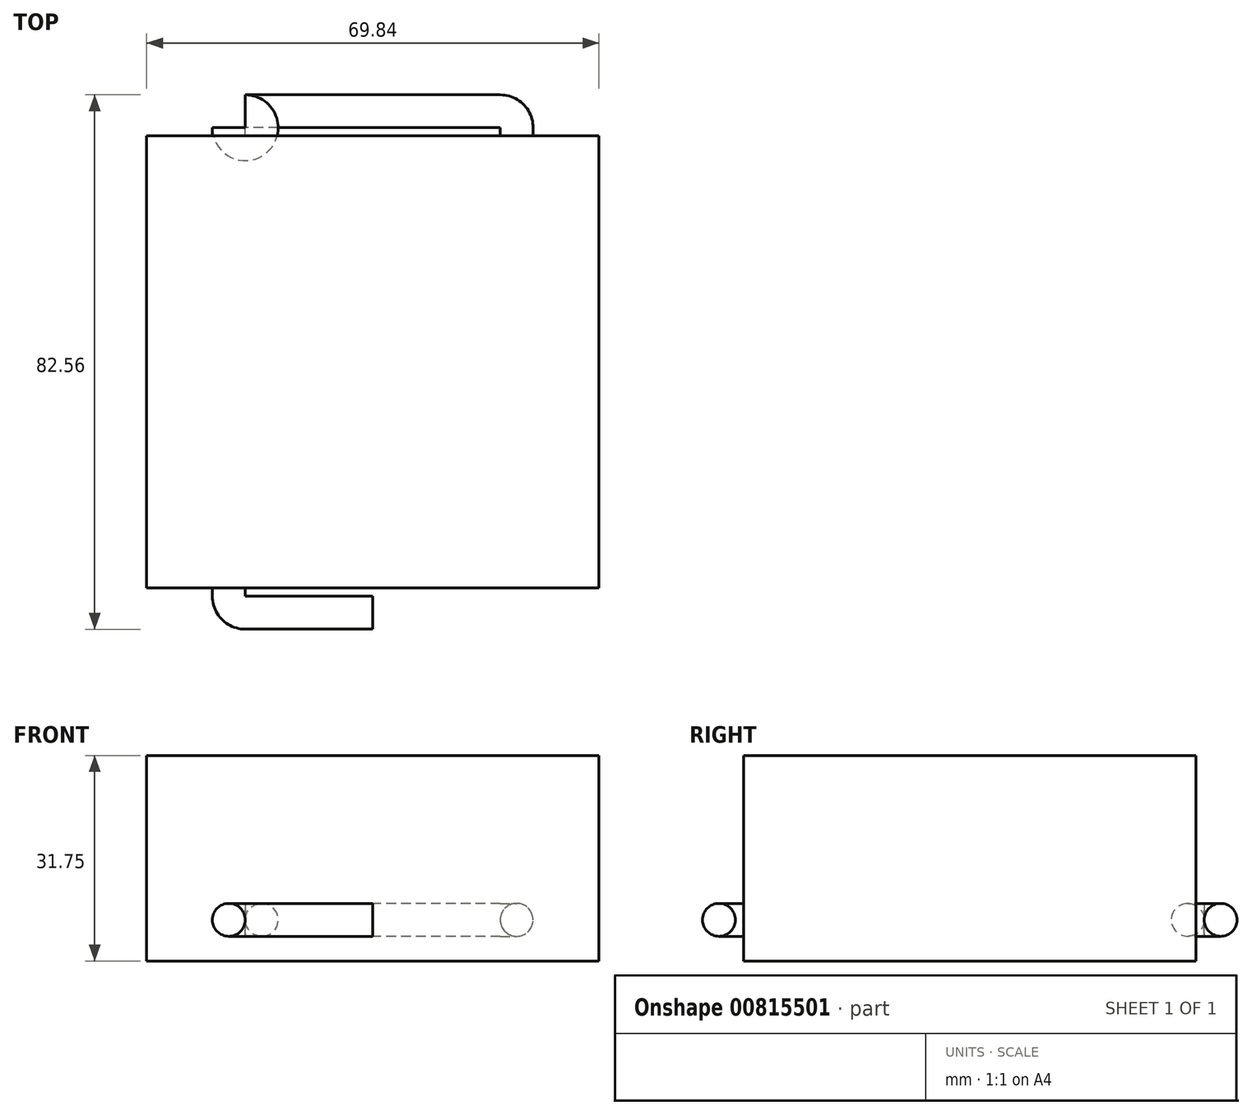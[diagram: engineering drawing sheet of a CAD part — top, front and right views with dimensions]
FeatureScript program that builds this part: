
annotation { "Feature Type Name" : "Feature", "Feature Type Description" : "" }
export const myFeature = defineFeature(function(context is Context, id is Id, definition is map)
    precondition{}
    {
        {
            var Q0;
            Q0=qCreatedBy(makeId("Top.planeOp"),FACE);
            var sketch = newSketch(context, id + "F0", { "sketchPlane" : qUnion([Q0])});
            skLineSegment(sketch, "E0.bottom", {"start": v(34.93, -34.92) * mm, "end": v(-34.92, -34.93) * mm});
            skLineSegment(sketch, "E0.top", {"start": v(34.92, 34.93) * mm, "end": v(-34.93, 34.93) * mm});
            skLineSegment(sketch, "E0.left", {"start": v(34.93, -34.92) * mm, "end": v(34.92, 34.93) * mm});
            skLineSegment(sketch, "E0.right", {"start": v(-34.92, -34.93) * mm, "end": v(-34.93, 34.93) * mm});
            skPoint(sketch, "E0.middle", {"position": v(0, 0) * mm});
            skSolve(sketch);
        }
        {
            var Q0;
            Q0 = qSketchRegion(id + "F0", true);
            extrude(context, id + "F1", {"entities" : qUnion([Q0]), "depth" : 31.75 * mm, "offsetDistance" : 25.4 * mm});
        }
        {
            var Q0;
            Q0=qCreatedBy(makeId("Top.planeOp"),FACE);
            cPlane(context, id + "F2", {"entities" : qUnion([Q0]), "cplaneType" : CPlaneType.OFFSET, "offset" : 6.35 * mm, "width" : 152.4 * mm, "height" : 152.4 * mm});
        }
        {
            var Q0;
            Q0=qCreatedBy(id+"F2.planeOp",FACE);
            var sketch = newSketch(context, id + "F3", { "sketchPlane" : qUnion([Q0])});
            skLineSegment(sketch, "E1", {"start": v(0, 0) * mm, "end": v(0, 38.73) * mm, "construction": true});
            skLineSegment(sketch, "E2", {"start": v(0, 38.73) * mm, "end": v(19.69, 38.73) * mm});
            skLineSegment(sketch, "E3", {"start": v(22.23, 36.2) * mm, "end": v(22.23, 34.92) * mm});
            skPoint(sketch, "E4.visualSharp", {"position": v(22.23, 38.73) * mm});
            skArc(sketch, "E4.filletArc", {"start": v(22.23, 36.2) * mm, "mid": v(21.48, 38) * mm, "end": v(19.69, 38.73) * mm});
            skSolve(sketch);
        }
        {
            var Q0;
            Q0=makeQuery(id+"F1.opExtrude","SWEPT_FACE",FACE,{"disambiguationData":[OSD([sQuery(id+"F0.wireOp",EDGE,"E0.top")])]});
            var sketch = newSketch(context, id + "F4", { "sketchPlane" : qUnion([Q0])});
            skLineSegment(sketch, "E5", {"start": v(0, 0) * mm, "end": v(0, 6.35) * mm, "construction": true});
            skLineSegment(sketch, "E6", {"start": v(0, 6.35) * mm, "end": v(-22.23, 6.35) * mm, "construction": true});
            skCircle(sketch, "E7", {"center": v(-22.23, 6.35) * mm, "radius": 2.54 * mm});
            skSolve(sketch);
        }
        {
            var Q0;
            Q0=makeQuery(id+"F4.imprint","IMPRINT",FACE,{"disambiguationData":[TD([[makeQuery(id+"F4.imprint","IMPRINT",EDGE,{"derivedFrom":sQuery(id+"F4.wireOp",EDGE,"E7")}),1.0]])]});
            var Q1;
            Q1 = qConstructionFilter(qBodyType(qCreatedBy(id + "F3" ,EDGE), BodyType.WIRE), ConstructionObject.NO);
            sweep(context, id + "F5", {"operationType" : NewBodyOperationType.ADD, "profiles" : qUnion([Q0]), "path" : qUnion([Q1])});
        }
        {
            var Q0;
            Q0=makeQuery(id+"F1.opExtrude","SWEPT_BODY",BODY,{"disambiguationData":[OSD([sQuery(id+"F0.wireOp",EDGE,"E0.bottom"),sQuery(id+"F0.wireOp",EDGE,"E0.top"),sQuery(id+"F0.wireOp",EDGE,"E0.left"),sQuery(id+"F0.wireOp",EDGE,"E0.right")])]});
            var Q1;
            Q1=makeQuery(id+"F5.opSweep","CAP_FACE",FACE,{"disambiguationData":[OSD([sQuery(id+"F3.wireOp",VERTEX,"E2.start"),sQuery(id+"F4.wireOp",EDGE,"E7")])],"isStart":false});
            mirror(context, id + "F6", {"entities" : qUnion([Q0]), "mirrorPlane" : qUnion([Q1])});
        }
        {
            var Q0;
            Q0=makeQuery(id+"F6.opPattern","COPY",BODY,{"derivedFrom":makeQuery(id+"F1.opExtrude","SWEPT_BODY",BODY,{"disambiguationData":[OSD([sQuery(id+"F0.wireOp",EDGE,"E0.bottom"),sQuery(id+"F0.wireOp",EDGE,"E0.top"),sQuery(id+"F0.wireOp",EDGE,"E0.left"),sQuery(id+"F0.wireOp",EDGE,"E0.right")])]}),"instanceName":"1"});
            var Q1;
            Q1=qCreatedBy(makeId("Front.planeOp"),FACE);
            mirror(context, id + "F7", {"operationType" : NewBodyOperationType.ADD, "entities" : qUnion([Q0]), "mirrorPlane" : qUnion([Q1])});
        }
    });
